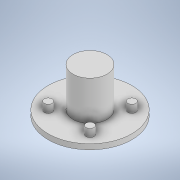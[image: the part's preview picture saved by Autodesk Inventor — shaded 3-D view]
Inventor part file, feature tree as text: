
AUTODESK INVENTOR PART (.ipt)
format: ipt  version: 2021 (Build 250183000, 183)  size: 133,120 bytes
history: native  units: mm
features: sketch x4, extrude x3, other x1
ambient origin geometry x8: Origin, YZ Plane, XZ Plane, XY Plane, X Axis, Y Axis, Z Axis, Center Point
bodies: Body1 (feature_tree)
feature tree (8):
  other  "Sólido1"
  extrude  "Extrusión1"  Depth=16.0mm
  sketch  "Boceto2"  dims[d2=3.0mm d3=40.0mm d5=360.0deg]
  extrude  "Extrusión2"  Depth=3.0mm TaperAngle=360.0deg
  extrude  "Extrusión3"  Depth=2.0mm TaperAngle=0.0deg
  sketch  "Boceto1"  dims[d0=16.0mm d1=16.0mm]
  sketch  "Boceto3"  dims[d7=32.0mm d8=2.0mm d9=0.0mm]
  sketch  "Boceto4"  dims[d10=13.0mm d11=15.0mm d12=0.0mm d13=5.0mm d14=0.0mm]
